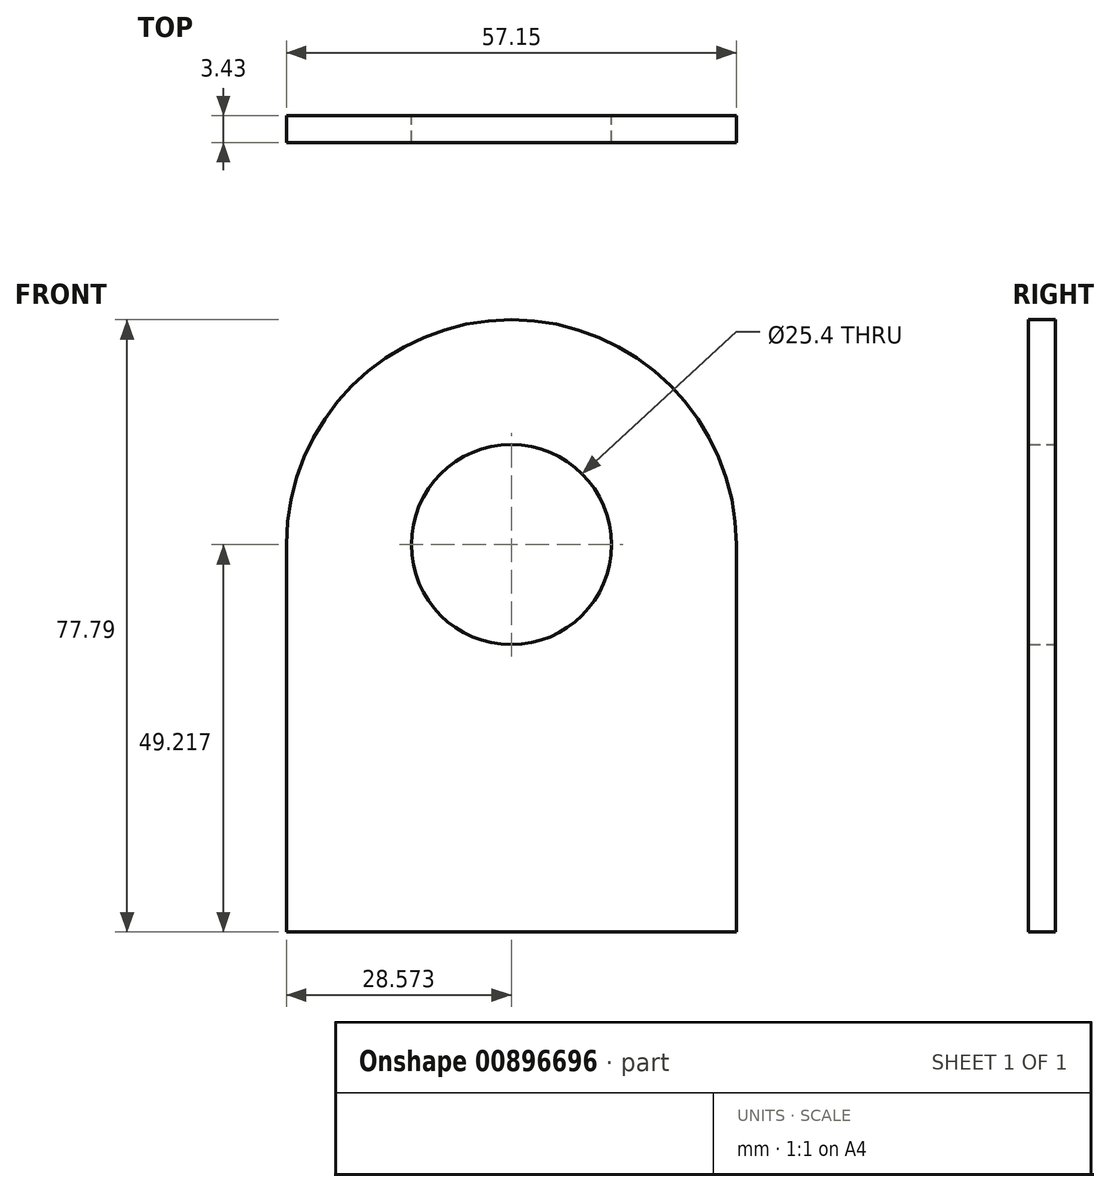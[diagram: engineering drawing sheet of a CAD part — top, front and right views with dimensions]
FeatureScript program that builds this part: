
annotation { "Feature Type Name" : "Feature", "Feature Type Description" : "" }
export const myFeature = defineFeature(function(context is Context, id is Id, definition is map)
    precondition{}
    {
        {
            var Q0;
            Q0=qCreatedBy(makeId("Front.planeOp"),FACE);
            var sketch = newSketch(context, id + "F0", { "sketchPlane" : qUnion([Q0])});
            skCircle(sketch, "E0", {"center": v(98.41, 485.59) * mm, "radius": 12.7 * mm});
            skLineSegment(sketch, "E1", {"start": v(126.99, 436.37) * mm, "end": v(126.99, 485.59) * mm});
            skLineSegment(sketch, "E2", {"start": v(69.84, 436.37) * mm, "end": v(126.99, 436.37) * mm});
            skLineSegment(sketch, "E3", {"start": v(69.84, 485.59) * mm, "end": v(69.84, 436.37) * mm});
            skArc(sketch, "E4", {"start": v(126.99, 485.59) * mm, "mid": v(98.41, 514.16) * mm, "end": v(69.84, 485.59) * mm});
            skSolve(sketch);
        }
        {
            var Q0;
            Q0 = qSketchRegion(id + "F0", true);
            extrude(context, id + "F1", {"entities" : qUnion([Q0]), "depth" : 3.43 * mm, "offsetDistance" : 25.4 * mm});
        }
    });
